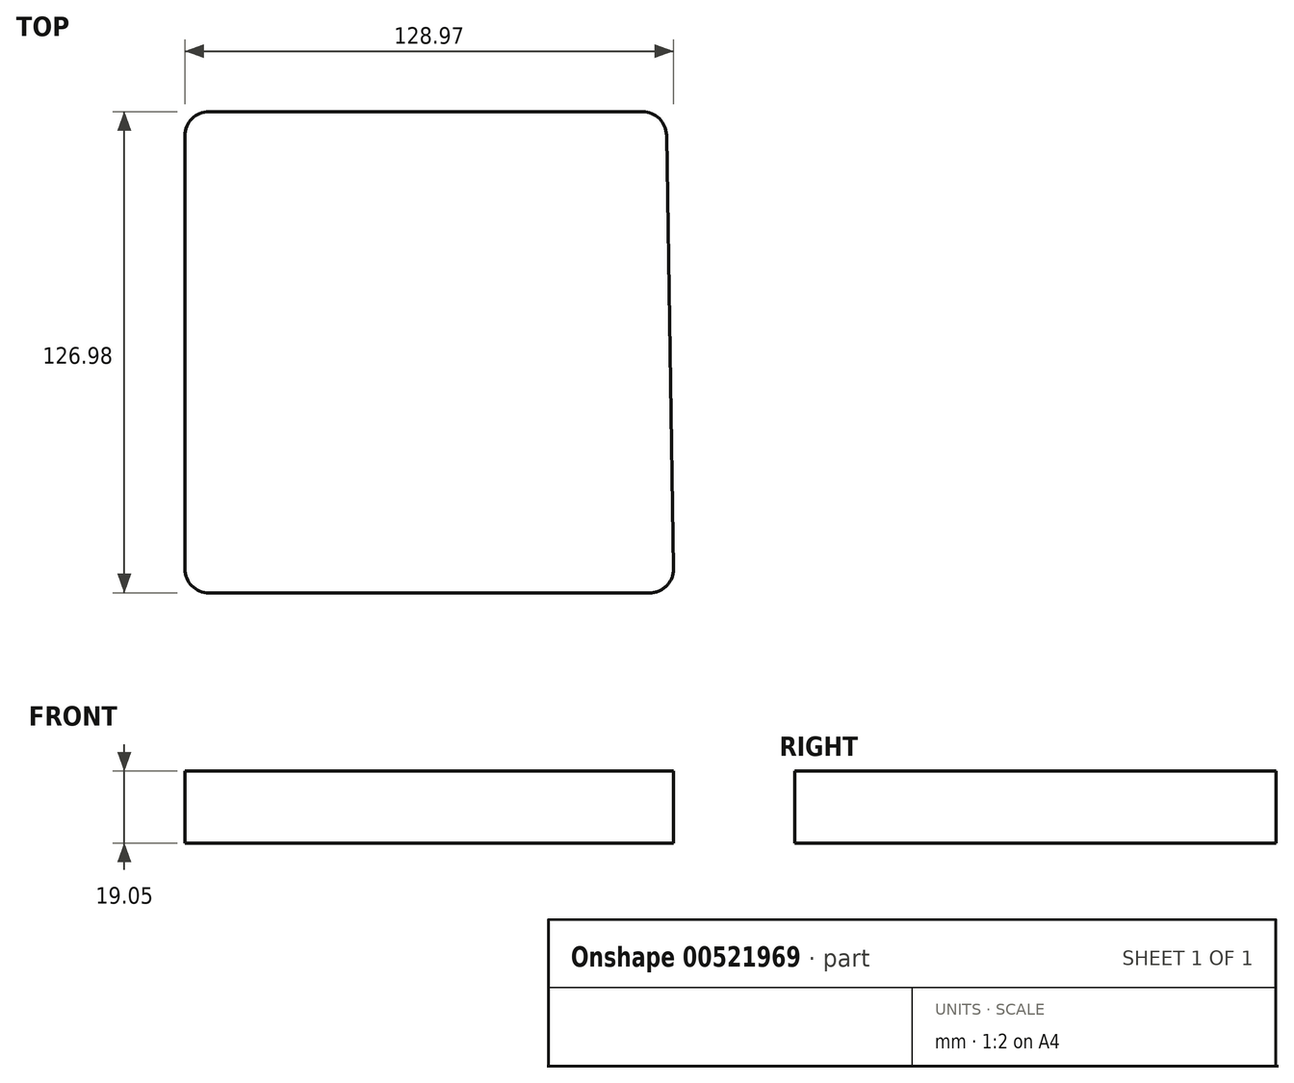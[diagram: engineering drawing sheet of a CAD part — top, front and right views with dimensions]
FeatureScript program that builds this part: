
annotation { "Feature Type Name" : "Feature", "Feature Type Description" : "" }
export const myFeature = defineFeature(function(context is Context, id is Id, definition is map)
    precondition{}
    {
        {
            var Q0;
            Q0=qCreatedBy(makeId("Top.planeOp"),FACE);
            var sketch = newSketch(context, id + "F0", { "sketchPlane" : qUnion([Q0])});
            skLineSegment(sketch, "E0", {"start": v(6.35, 0) * mm, "end": v(122.62, 0) * mm});
            skLineSegment(sketch, "E1", {"start": v(128.97, 6.45) * mm, "end": v(127.1, 120.74) * mm});
            skLineSegment(sketch, "E2", {"start": v(0, 6.35) * mm, "end": v(0, 120.63) * mm});
            skLineSegment(sketch, "E3", {"start": v(6.35, 126.98) * mm, "end": v(120.75, 126.98) * mm});
            skPoint(sketch, "E4.visualSharp", {"position": v(0, 126.98) * mm});
            skArc(sketch, "E4.filletArc", {"start": v(6.35, 126.98) * mm, "mid": v(1.86, 125.12) * mm, "end": v(0, 120.63) * mm});
            skPoint(sketch, "E5.visualSharp", {"position": v(127, 126.98) * mm});
            skArc(sketch, "E5.filletArc", {"start": v(127.1, 120.74) * mm, "mid": v(125.2, 125.16) * mm, "end": v(120.75, 126.98) * mm});
            skPoint(sketch, "E6.visualSharp", {"position": v(0, 0) * mm});
            skArc(sketch, "E6.filletArc", {"start": v(0, 6.35) * mm, "mid": v(1.86, 1.86) * mm, "end": v(6.35, 0) * mm});
            skPoint(sketch, "E7.visualSharp", {"position": v(129.08, 0) * mm});
            skArc(sketch, "E7.filletArc", {"start": v(122.62, 0) * mm, "mid": v(127.15, 1.9) * mm, "end": v(128.97, 6.45) * mm});
            skSolve(sketch);
        }
        {
            var Q0;
            Q0 = qSketchRegion(id + "F0", true);
            var Q1;
            Q1=makeQuery(id+"F0.imprint","IMPRINT",FACE,{"disambiguationData":[TD([[makeQuery(id+"F0.imprint","IMPRINT",EDGE,{"derivedFrom":sQuery(id+"F0.wireOp",EDGE,"E0")}),1.0]])]});
            extrude(context, id + "F1", {"entities" : qUnion([Q0, Q1]), "depth" : 19.05 * mm, "offsetDistance" : 25.4 * mm});
        }
    });
